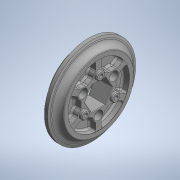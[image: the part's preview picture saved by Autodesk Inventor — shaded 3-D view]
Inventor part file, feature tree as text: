
AUTODESK INVENTOR PART (.ipt)
format: ipt  version: 2020 (Build 240168000, 168)  size: 656,896 bytes
history: native  units: mm (DEFAULTED — no unit token found)
features: mirror x1
ambient origin geometry x8: Origin, YZ Plane, XZ Plane, XY Plane, X Axis, Y Axis, Z Axis, Center Point
bodies: Solid1 (feature_tree)
feature tree (1):
  mirror  "Mirror5"
